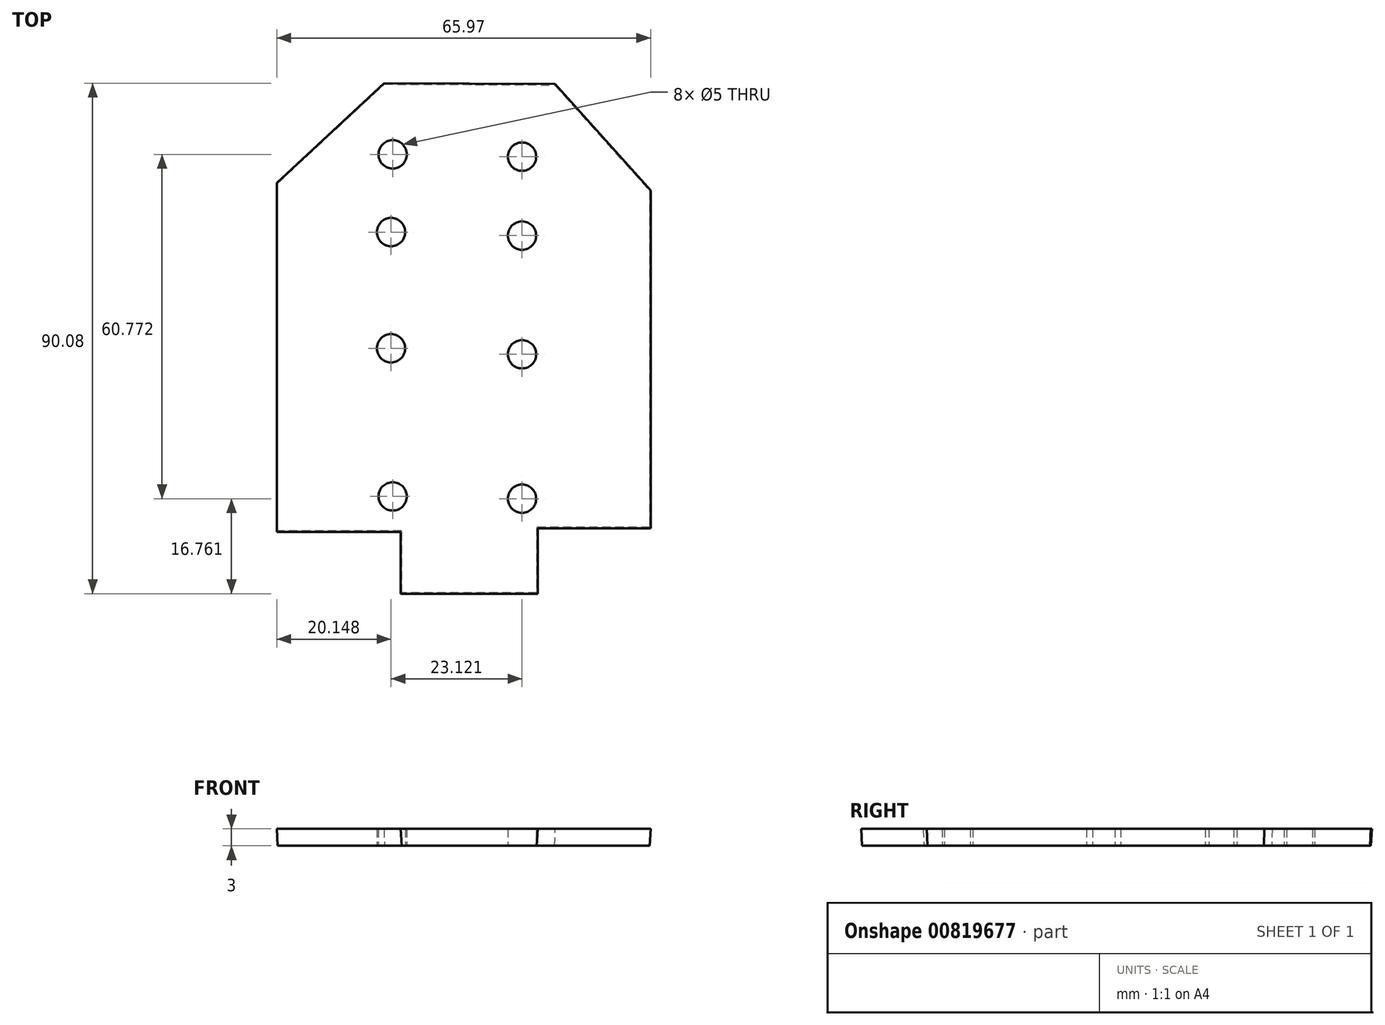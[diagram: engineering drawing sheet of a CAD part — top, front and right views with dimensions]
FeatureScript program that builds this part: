
annotation { "Feature Type Name" : "Feature", "Feature Type Description" : "" }
export const myFeature = defineFeature(function(context is Context, id is Id, definition is map)
    precondition{}
    {
        {
            var Q0;
            Q0=qCreatedBy(makeId("Top.planeOp"),FACE);
            var sketch = newSketch(context, id + "F0", { "sketchPlane" : qUnion([Q0])});
            skLineSegment(sketch, "E0", {"start": v(9.94, -24.66) * mm, "end": v(-13.92, -24.66) * mm});
            skLineSegment(sketch, "E1", {"start": v(9.94, -24.66) * mm, "end": v(9.94, -13.1) * mm});
            skLineSegment(sketch, "E2", {"start": v(-13.92, -24.66) * mm, "end": v(-13.92, -13.74) * mm});
            skLineSegment(sketch, "E3", {"start": v(9.94, -13.1) * mm, "end": v(29.87, -13.1) * mm});
            skLineSegment(sketch, "E4", {"start": v(-13.92, -13.74) * mm, "end": v(-35.78, -13.74) * mm});
            skLineSegment(sketch, "E5", {"start": v(29.87, -13.1) * mm, "end": v(29.87, 46.26) * mm});
            skLineSegment(sketch, "E6", {"start": v(-35.78, -13.74) * mm, "end": v(-35.78, 47.63) * mm});
            skLineSegment(sketch, "E7", {"start": v(29.87, 46.26) * mm, "end": v(13.1, 64.95) * mm});
            skLineSegment(sketch, "E8", {"start": v(-35.78, 47.63) * mm, "end": v(-16.95, 65.1) * mm});
            skLineSegment(sketch, "E9", {"start": v(-16.95, 65.1) * mm, "end": v(13.1, 64.95) * mm});
            skSolve(sketch);
        }
        {
            var Q0;
            Q0=makeQuery(id+"F0.imprint","IMPRINT",FACE,{"disambiguationData":[TD([[makeQuery(id+"F0.imprint","IMPRINT",EDGE,{"derivedFrom":sQuery(id+"F0.wireOp",EDGE,"E0")}),-1.0]])]});
            var sketch = newSketch(context, id + "F1", { "sketchPlane" : qUnion([Q0])});
            skSolve(sketch);
        }
        {
            var Q0;
            Q0=makeQuery(id+"F0.imprint","IMPRINT",FACE,{"disambiguationData":[TD([[makeQuery(id+"F0.imprint","IMPRINT",EDGE,{"derivedFrom":sQuery(id+"F0.wireOp",EDGE,"E0")}),-1.0]])]});
            extrude(context, id + "F2", {"entities" : qUnion([Q0]), "depth" : 3 * mm, "offsetDistance" : 25.4 * mm, "hasDraft" : true, "draftAngle" : 3 * degree});
        }
        {
            var Q0;
            Q0=makeQuery(id+"F2.opExtrude","CAP_FACE",FACE,{"disambiguationData":[OSD([sQuery(id+"F0.wireOp",EDGE,"E0"),sQuery(id+"F0.wireOp",EDGE,"E1"),sQuery(id+"F0.wireOp",EDGE,"E2"),sQuery(id+"F0.wireOp",EDGE,"E3"),sQuery(id+"F0.wireOp",EDGE,"E4"),sQuery(id+"F0.wireOp",EDGE,"E5"),sQuery(id+"F0.wireOp",EDGE,"E6"),sQuery(id+"F0.wireOp",EDGE,"E7"),sQuery(id+"F0.wireOp",EDGE,"E8"),sQuery(id+"F0.wireOp",EDGE,"E9")])],"isStart":false});
            var sketch = newSketch(context, id + "F3", { "sketchPlane" : qUnion([Q0])});
            skSolve(sketch);
        }
        {
            var Q0;
            Q0=qCreatedBy(makeId("Top.planeOp"),FACE);
            var sketch = newSketch(context, id + "F4", { "sketchPlane" : qUnion([Q0])});
            skLineSegment(sketch, "E10", {"start": v(-15.8, 0) * mm, "end": v(-15.8, 54.11) * mm});
            skPoint(sketch, "E11", {"position": v(-15.8, 54.11) * mm});
            skPoint(sketch, "E12", {"position": v(-15.8, 0) * mm});
            skPoint(sketch, "E13", {"position": v(-15.8, 39) * mm});
            skPoint(sketch, "E14", {"position": v(-15.8, 18.49) * mm});
            skSolve(sketch);
        }
        {
            var Q0;
            Q0=qCreatedBy(makeId("Top.planeOp"),FACE);
            var sketch = newSketch(context, id + "F5", { "sketchPlane" : qUnion([Q0])});
            skLineSegment(sketch, "E15", {"start": v(-15.5, 52.71) * mm, "end": v(-15.5, -7.65) * mm});
            skLineSegment(sketch, "E16", {"start": v(7.33, 52.3) * mm, "end": v(7.33, -8.06) * mm});
            skPoint(sketch, "E17", {"position": v(7.33, 52.3) * mm});
            skPoint(sketch, "E18", {"position": v(7.33, 38.38) * mm});
            skPoint(sketch, "E19", {"position": v(7.33, 17.43) * mm});
            skPoint(sketch, "E20", {"position": v(-15.5, -7.65) * mm});
            skPoint(sketch, "E21", {"position": v(7.33, -8.06) * mm});
            skPoint(sketch, "E22", {"position": v(-15.5, 52.71) * mm});
            skSolve(sketch);
        }
        {
            var Q0;
            Q0=sQuery(id+"F5.wireOp",VERTEX,"E22");
            var Q1;
            Q1=sQuery(id+"F5.wireOp",VERTEX,"E17");
            var Q2;
            Q2=sQuery(id+"F4.wireOp",VERTEX,"E13");
            var Q3;
            Q3=sQuery(id+"F5.wireOp",VERTEX,"E18");
            var Q4;
            Q4=sQuery(id+"F4.wireOp",VERTEX,"E14");
            var Q5;
            Q5=sQuery(id+"F5.wireOp",VERTEX,"E19");
            var Q6;
            Q6=sQuery(id+"F5.wireOp",VERTEX,"E20");
            var Q7;
            Q7=sQuery(id+"F5.wireOp",VERTEX,"E21");
            var Q8;
            Q8=makeQuery(id+"F2.opExtrude","SWEPT_BODY",BODY,{"disambiguationData":[OSD([sQuery(id+"F0.wireOp",EDGE,"E0"),sQuery(id+"F0.wireOp",EDGE,"E1"),sQuery(id+"F0.wireOp",EDGE,"E2"),sQuery(id+"F0.wireOp",EDGE,"E3"),sQuery(id+"F0.wireOp",EDGE,"E4"),sQuery(id+"F0.wireOp",EDGE,"E5"),sQuery(id+"F0.wireOp",EDGE,"E6"),sQuery(id+"F0.wireOp",EDGE,"E7"),sQuery(id+"F0.wireOp",EDGE,"E8"),sQuery(id+"F0.wireOp",EDGE,"E9")])]});
            hole(context, id + "F6", {"style" : HoleStyle.SIMPLE, "endStyle" : HoleEndStyle.THROUGH, "oppositeDirection" : true, "holeDiameter" : 5 * mm, "majorDiameter" : 5 * mm, "isTappedThrough" : true, "tappedDepth" : 12 * mm, "tapClearance" : 3, "locations" : qUnion([Q0, Q1, Q2, Q3, Q4, Q5, Q6, Q7]), "scope" : qUnion([Q8])});
        }
        {
            var Q0;
            Q0=qCreatedBy(makeId("Top.planeOp"),FACE);
            var sketch = newSketch(context, id + "F7", { "sketchPlane" : qUnion([Q0])});
            skEllipse(sketch, "E23", {"center": v(-26.27, 17.48) * mm, "majorRadius": 21.14 * mm, "minorRadius": 6.38 * mm, "majorAxis": v(0, 1)});
            skSolve(sketch);
        }
        {
            var Q0;
            Q0=qCreatedBy(makeId("Top.planeOp"),FACE);
            var sketch = newSketch(context, id + "F8", { "sketchPlane" : qUnion([Q0])});
            skEllipse(sketch, "E24", {"center": v(19.36, 17.06) * mm, "majorRadius": 21.68 * mm, "minorRadius": 5.74 * mm, "majorAxis": v(0, 1)});
            skSolve(sketch);
        }
        {
            var Q0;
            Q0=sQuery(id+"F7.wireOp",EDGE,"E23");
            var Q1;
            Q1=sQuery(id+"F8.wireOp",EDGE,"E24");
            extrude(context, id + "F9", {"bodyType" : ToolBodyType.SURFACE, "surfaceEntities" : qUnion([Q0, Q1]), "endBound" : BoundingType.UP_TO_NEXT, "depth" : 25 * mm, "offsetDistance" : 25 * mm});
        }
    });
